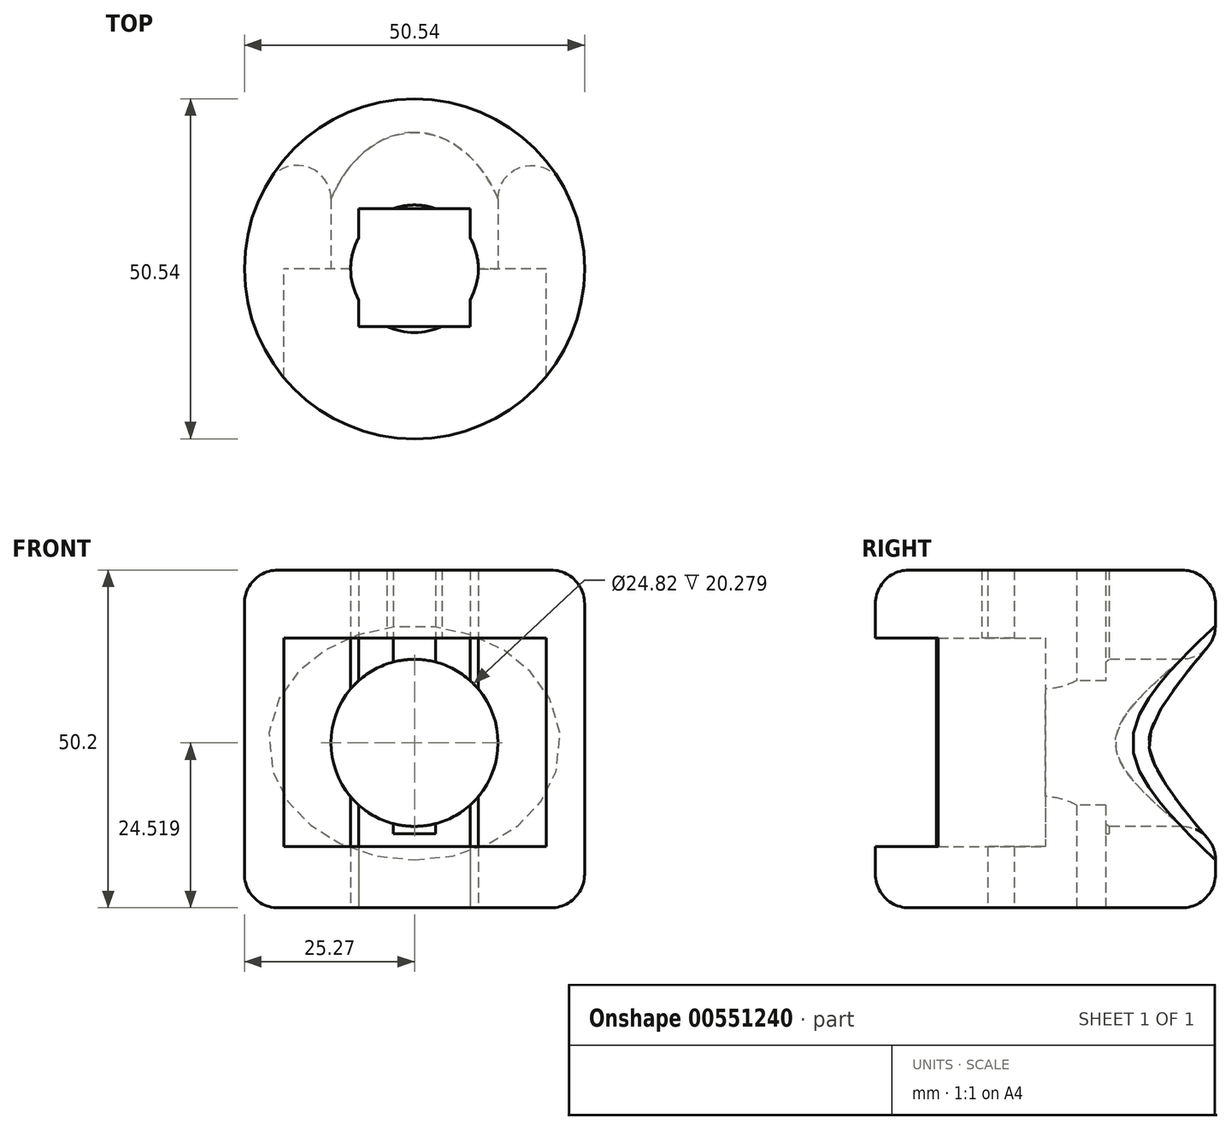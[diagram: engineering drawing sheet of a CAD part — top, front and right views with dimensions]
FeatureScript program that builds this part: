
annotation { "Feature Type Name" : "Feature", "Feature Type Description" : "" }
export const myFeature = defineFeature(function(context is Context, id is Id, definition is map)
    precondition{}
    {
        {
            var Q0;
            Q0=qCreatedBy(makeId("Top.planeOp"),FACE);
            var sketch = newSketch(context, id + "F0", { "sketchPlane" : qUnion([Q0])});
            skCircle(sketch, "E0", {"center": v(0, 0) * mm, "radius": 25.27 * mm});
            skSolve(sketch);
        }
        {
            var Q0;
            Q0 = qSketchRegion(id + "F0", true);
            extrude(context, id + "F1", {"entities" : qUnion([Q0]), "depth" : 50.2 * mm, "offsetDistance" : 25 * mm});
        }
        {
            var Q0;
            Q0=makeQuery(id+"F1.opExtrude","SWEPT_FACE",FACE,{"disambiguationData":[OSD([sQuery(id+"F0.wireOp",EDGE,"E0")])]});
            fillet(context, id + "F2", {"entities" : qUnion([Q0]), "radius" : 5 * mm, "tangentPropagation" : true, "allowEdgeOverflow" : false});
        }
        {
            var Q0;
            Q0=qCreatedBy(makeId("Top.planeOp"),FACE);
            var sketch = newSketch(context, id + "F3", { "sketchPlane" : qUnion([Q0])});
            skCircle(sketch, "E1", {"center": v(0, 0) * mm, "radius": 9.48 * mm});
            skSolve(sketch);
        }
        {
            var Q0;
            Q0 = qSketchRegion(id + "F3", true);
            extrude(context, id + "F4", {"entities" : qUnion([Q0]), "operationType" : NewBodyOperationType.REMOVE, "depth" : 67 * mm, "offsetDistance" : 25 * mm});
        }
        {
            var Q0;
            Q0=qCreatedBy(makeId("Top.planeOp"),FACE);
            var sketch = newSketch(context, id + "F5", { "sketchPlane" : qUnion([Q0])});
            skLineSegment(sketch, "E2.bottom", {"start": v(-8.08, 10.29) * mm, "end": v(8.27, 10.29) * mm});
            skLineSegment(sketch, "E2.top", {"start": v(-8.08, -10.48) * mm, "end": v(8.27, -10.48) * mm});
            skLineSegment(sketch, "E2.left", {"start": v(-8.08, 10.29) * mm, "end": v(-8.08, -10.48) * mm});
            skLineSegment(sketch, "E2.right", {"start": v(8.27, 10.29) * mm, "end": v(8.27, -10.48) * mm});
            skSolve(sketch);
        }
        {
            var Q0;
            Q0 = qSketchRegion(id + "F5", true);
            extrude(context, id + "F6", {"entities" : qUnion([Q0]), "operationType" : NewBodyOperationType.ADD, "depth" : 11 * mm, "offsetDistance" : 25 * mm});
        }
        {
            var Q0;
            Q0=qCreatedBy(makeId("Top.planeOp"),FACE);
            var sketch = newSketch(context, id + "F7", { "sketchPlane" : qUnion([Q0])});
            skLineSegment(sketch, "E3.bottom", {"start": v(-8.27, -8.56) * mm, "end": v(8.27, -8.56) * mm});
            skLineSegment(sketch, "E3.top", {"start": v(-8.27, 8.94) * mm, "end": v(8.27, 8.94) * mm});
            skLineSegment(sketch, "E3.left", {"start": v(-8.27, -8.56) * mm, "end": v(-8.27, 8.94) * mm});
            skLineSegment(sketch, "E3.right", {"start": v(8.27, -8.56) * mm, "end": v(8.27, 8.94) * mm});
            skSolve(sketch);
        }
        {
            var Q0;
            Q0 = qSketchRegion(id + "F7", true);
            extrude(context, id + "F8", {"entities" : qUnion([Q0]), "operationType" : NewBodyOperationType.REMOVE, "depth" : 79.8 * mm, "offsetDistance" : 25 * mm});
        }
        {
            var Q0;
            Q0=qCreatedBy(makeId("Front.planeOp"),FACE);
            var sketch = newSketch(context, id + "F9", { "sketchPlane" : qUnion([Q0])});
            skLineSegment(sketch, "E4.bottom", {"start": v(19.62, 40.1) * mm, "end": v(-19.42, 40.1) * mm});
            skLineSegment(sketch, "E4.top", {"start": v(19.62, 9.13) * mm, "end": v(-19.42, 9.13) * mm});
            skLineSegment(sketch, "E4.left", {"start": v(19.62, 40.1) * mm, "end": v(19.62, 9.13) * mm});
            skLineSegment(sketch, "E4.right", {"start": v(-19.42, 40.1) * mm, "end": v(-19.42, 9.13) * mm});
            skSolve(sketch);
        }
        {
            var Q0;
            Q0 = qSketchRegion(id + "F9", true);
            extrude(context, id + "F10", {"entities" : qUnion([Q0]), "operationType" : NewBodyOperationType.REMOVE, "depth" : 41.1 * mm, "offsetDistance" : 25 * mm});
        }
        {
            var Q0;
            Q0=qCreatedBy(makeId("Front.planeOp"),FACE);
            var sketch = newSketch(context, id + "F11", { "sketchPlane" : qUnion([Q0])});
            skCircle(sketch, "E5", {"center": v(0, 24.52) * mm, "radius": 12.41 * mm});
            skSolve(sketch);
        }
        {
            var Q0;
            Q0 = qSketchRegion(id + "F11", true);
            extrude(context, id + "F12", {"entities" : qUnion([Q0]), "operationType" : NewBodyOperationType.REMOVE, "oppositeDirection" : true, "depth" : 44.3 * mm, "offsetDistance" : 25 * mm});
        }
        {
            var Q0;
            Q0=makeQuery(id+"F12.boolean.opBoolean","INTERSECT",EDGE,{"derivedFrom":[makeQuery(id+"F1.opExtrude","SWEPT_FACE",FACE,{"disambiguationData":[OSD([sQuery(id+"F0.wireOp",EDGE,"E0")])]}),makeQuery(id+"F12.opExtrude","SWEPT_FACE",FACE,{"disambiguationData":[OSD([sQuery(id+"F11.wireOp",EDGE,"E5")])]})]});
            fillet(context, id + "F13", {"entities" : qUnion([Q0]), "radius" : 5 * mm, "tangentPropagation" : true, "allowEdgeOverflow" : false});
        }
    });
